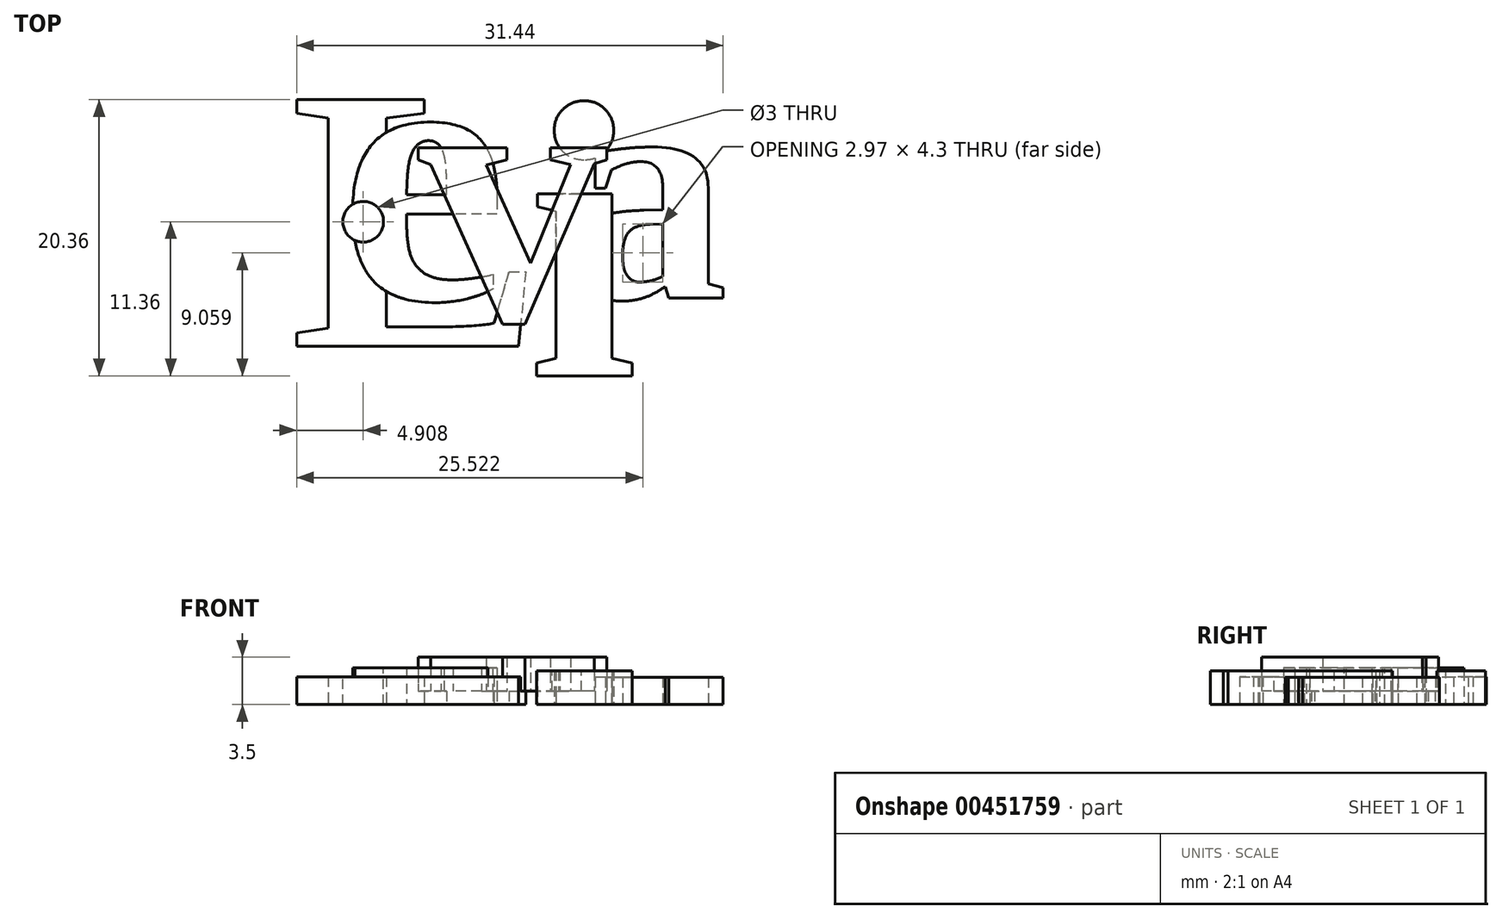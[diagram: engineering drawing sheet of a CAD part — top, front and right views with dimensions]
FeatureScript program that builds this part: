
annotation { "Feature Type Name" : "Feature", "Feature Type Description" : "" }
export const myFeature = defineFeature(function(context is Context, id is Id, definition is map)
    precondition{}
    {
        {
            var Q0;
            Q0=qCreatedBy(makeId("Top.planeOp"),FACE);
            var sketch = newSketch(context, id + "F0", { "sketchPlane" : qUnion([Q0])});
            skText(sketch, "E0", { "text": "L", "fontName": "Tinos-Bold.ttf"});
            skLineSegment(sketch, "E1", {"start": v(0, 7.79) * mm, "end": v(0, -16.87) * mm, "construction": true});
            const initialGuessF0  = {"E0": [-0.02041, -0.00172, 1, 0, 0.02]};
            skSetInitialGuess(sketch, initialGuessF0);
            skSolve(sketch);
        }
        {
            var Q0;
            Q0 = qSketchRegion(id + "F0", true);
            extrude(context, id + "F1", {"entities" : qUnion([Q0]), "depth" : 2.05 * mm});
        }
        {
            var Q0;
            Q0=qCreatedBy(makeId("Top.planeOp"),FACE);
            var sketch = newSketch(context, id + "F2", { "sketchPlane" : qUnion([Q0])});
            skText(sketch, "E2", { "text": "e", "fontName": "Tinos-Bold.ttf"});
            const initialGuessF2  = {"E2": [-0.01676, 0.00176, 1, 0, 0.02]};
            skSetInitialGuess(sketch, initialGuessF2);
            skSolve(sketch);
        }
        {
            var Q0;
            Q0 = qSketchRegion(id + "F2", true);
            extrude(context, id + "F3", {"entities" : qUnion([Q0]), "operationType" : NewBodyOperationType.ADD, "depth" : 2.7 * mm});
        }
        {
            var Q0;
            Q0=qCreatedBy(makeId("Top.planeOp"),FACE);
            var sketch = newSketch(context, id + "F4", { "sketchPlane" : qUnion([Q0])});
            skText(sketch, "E3", { "text": "v", "fontName": "Tinos-Bold.ttf"});
            const initialGuessF4  = {"E3": [-0.01096, 0.00017, 1, 0, 0.02]};
            skSetInitialGuess(sketch, initialGuessF4);
            skSolve(sketch);
        }
        {
            var Q0;
            Q0 = qSketchRegion(id + "F4", true);
            extrude(context, id + "F5", {"entities" : qUnion([Q0]), "operationType" : NewBodyOperationType.ADD, "depth" : 3.5 * mm, "hasSecondDirection" : true, "secondDirectionOppositeDirection" : false, "secondDirectionDepth" : 1 * mm});
        }
        {
            var Q0;
            Q0=qCreatedBy(makeId("Top.planeOp"),FACE);
            var sketch = newSketch(context, id + "F6", { "sketchPlane" : qUnion([Q0])});
            skText(sketch, "E4", { "text": "i", "fontName": "Tinos-Bold.ttf"});
            const initialGuessF6  = {"E4": [-0.0029, -0.00389, 1, 0, 0.02105]};
            skSetInitialGuess(sketch, initialGuessF6);
            skSolve(sketch);
        }
        {
            var Q0;
            Q0 = qSketchRegion(id + "F6", true);
            extrude(context, id + "F7", {"entities" : qUnion([Q0]), "operationType" : NewBodyOperationType.ADD, "depth" : 2.5 * mm});
        }
        {
            var Q0;
            Q0=qCreatedBy(makeId("Top.planeOp"),FACE);
            var sketch = newSketch(context, id + "F8", { "sketchPlane" : qUnion([Q0])});
            skText(sketch, "E5", { "text": "a", "fontName": "Tinos-Bold.ttf"});
            const initialGuessF8  = {"E5": [0, 0.00185, 1, 0, 0.01708]};
            skSetInitialGuess(sketch, initialGuessF8);
            skSolve(sketch);
        }
        {
            var Q0;
            Q0 = qSketchRegion(id + "F8", true);
            extrude(context, id + "F9", {"entities" : qUnion([Q0]), "operationType" : NewBodyOperationType.ADD, "depth" : 2 * mm});
        }
        {
            var Q0;
            Q0=makeQuery(id+"F3.opExtrude","CAP_FACE",FACE,{"disambiguationData":[OSD([sQuery(id+"F2.wireOp",EDGE,"E2.sketch_text.stroke-0"),sQuery(id+"F2.wireOp",EDGE,"E2.sketch_text.stroke-1"),sQuery(id+"F2.wireOp",EDGE,"E2.sketch_text.stroke-2"),sQuery(id+"F2.wireOp",EDGE,"E2.sketch_text.stroke-3"),sQuery(id+"F2.wireOp",EDGE,"E2.sketch_text.stroke-4"),sQuery(id+"F2.wireOp",EDGE,"E2.sketch_text.stroke-5"),sQuery(id+"F2.wireOp",EDGE,"E2.sketch_text.stroke-6"),sQuery(id+"F2.wireOp",EDGE,"E2.sketch_text.stroke-7"),sQuery(id+"F2.wireOp",EDGE,"E2.sketch_text.stroke-8"),sQuery(id+"F2.wireOp",EDGE,"E2.sketch_text.stroke-9"),sQuery(id+"F2.wireOp",EDGE,"E2.sketch_text.stroke-10"),sQuery(id+"F2.wireOp",EDGE,"E2.sketch_text.stroke-11"),sQuery(id+"F2.wireOp",EDGE,"E2.sketch_text.stroke-12"),sQuery(id+"F2.wireOp",EDGE,"E2.sketch_text.stroke-13"),sQuery(id+"F2.wireOp",EDGE,"E2.sketch_text.stroke-14"),sQuery(id+"F2.wireOp",EDGE,"E2.sketch_text.stroke-15"),sQuery(id+"F2.wireOp",EDGE,"E2.sketch_text.stroke-16"),sQuery(id+"F2.wireOp",EDGE,"E2.sketch_text.stroke-17"),sQuery(id+"F2.wireOp",EDGE,"E2.sketch_text.stroke-18"),sQuery(id+"F2.wireOp",EDGE,"E2.sketch_text.stroke-19"),sQuery(id+"F2.wireOp",EDGE,"E2.sketch_text.stroke-20"),sQuery(id+"F2.wireOp",EDGE,"E2.sketch_text.stroke-21")])],"isStart":false});
            var sketch = newSketch(context, id + "F10", { "sketchPlane" : qUnion([Q0])});
            skCircle(sketch, "E6", {"center": v(-15.03, 7.47) * mm, "radius": 1.5 * mm});
            skSolve(sketch);
        }
        {
            var Q0;
            Q0 = qSketchRegion(id + "F10", true);
            extrude(context, id + "F11", {"entities" : qUnion([Q0]), "operationType" : NewBodyOperationType.REMOVE, "endBound" : BoundingType.THROUGH_ALL, "oppositeDirection" : true, "depth" : 25 * mm});
        }
    });
